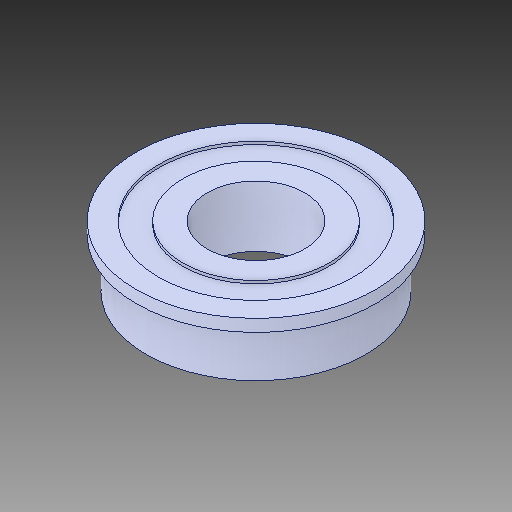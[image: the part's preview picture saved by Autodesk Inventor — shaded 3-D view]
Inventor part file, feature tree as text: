
AUTODESK INVENTOR PART (.ipt)
format: ipt  version: 2018 (Build 220112000, 112)  size: 122,880 bytes
history: native  units: in
note: dims shown in document units (in); Inventor stores cm internally (conversion verified against a paired STEP export)
features: revolve x1
ambient origin geometry x8: Origin, YZ Plane, XZ Plane, XY Plane, X Axis, Y Axis, Z Axis, Center Point
bodies: Solid1 (feature_tree)
feature tree (1):
  revolve  "Revolve1"  [1 undecoded]
note: 1 required parameter value undecoded (feature->parameter linkage not recoverable at this tier; creation-order binding heuristic only, values carry confidence <= 0.55)
